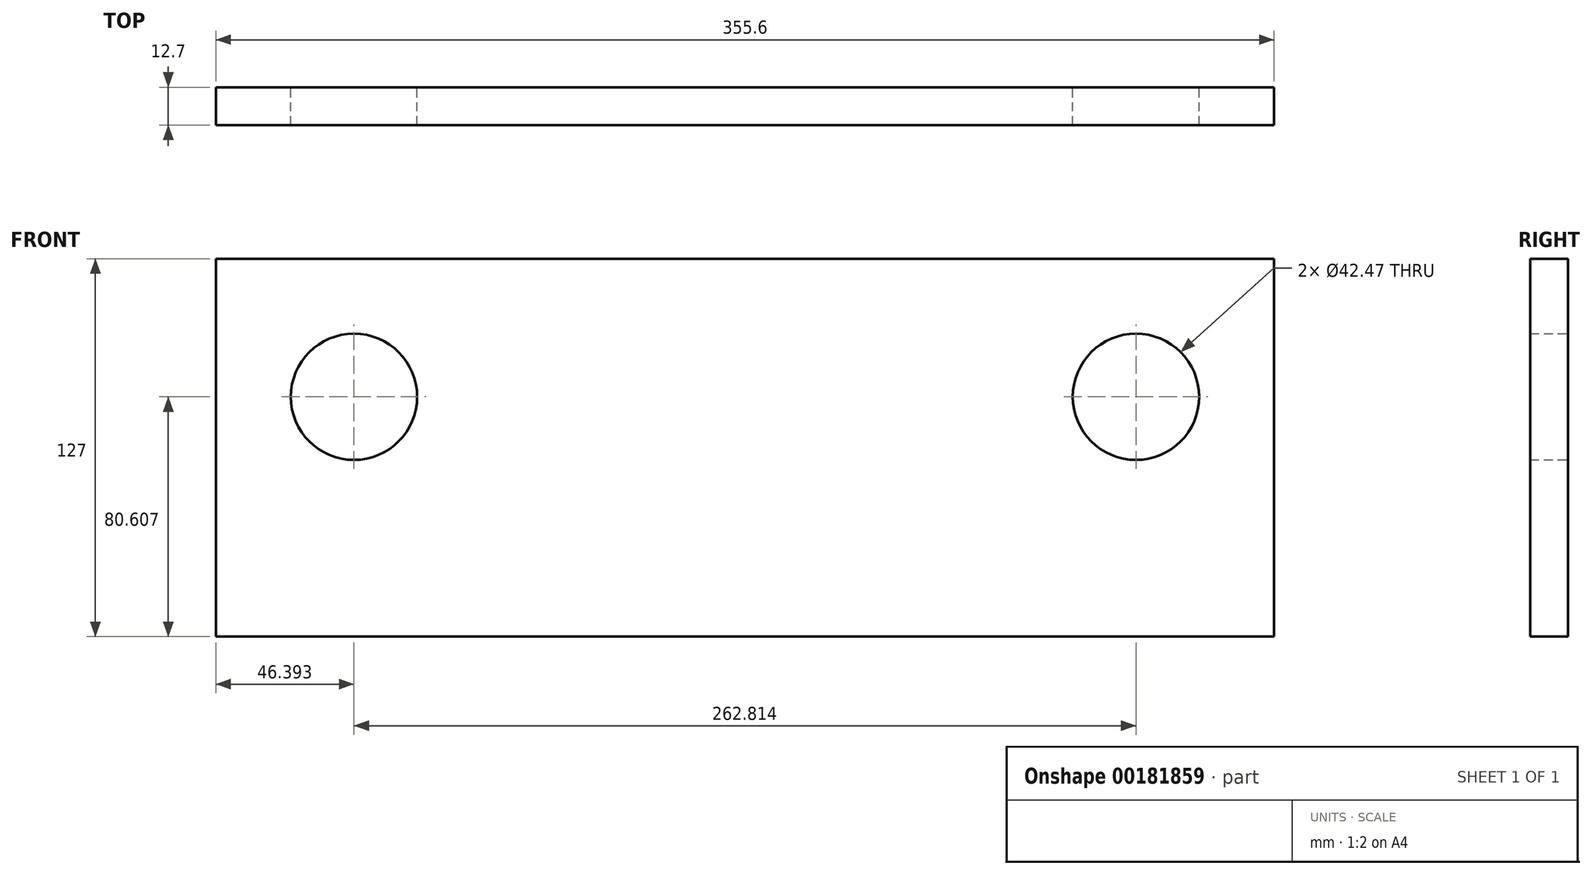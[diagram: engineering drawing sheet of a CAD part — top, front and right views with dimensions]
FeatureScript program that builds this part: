
annotation { "Feature Type Name" : "Feature", "Feature Type Description" : "" }
export const myFeature = defineFeature(function(context is Context, id is Id, definition is map)
    precondition{}
    {
        {
            var Q0;
            Q0=qCreatedBy(makeId("Front.planeOp"),FACE);
            var sketch = newSketch(context, id + "F0", { "sketchPlane" : qUnion([Q0])});
            skLineSegment(sketch, "E0.bottom", {"start": v(177.8, 63.5) * mm, "end": v(-177.8, 63.5) * mm});
            skLineSegment(sketch, "E0.top", {"start": v(177.8, -63.5) * mm, "end": v(-177.8, -63.5) * mm});
            skLineSegment(sketch, "E0.left", {"start": v(177.8, 63.5) * mm, "end": v(177.8, -63.5) * mm});
            skLineSegment(sketch, "E0.right", {"start": v(-177.8, 63.5) * mm, "end": v(-177.8, -63.5) * mm});
            skPoint(sketch, "E0.middle", {"position": v(0, 0) * mm});
            skLineSegment(sketch, "E1.bottom", {"start": v(177.8, 63.5) * mm, "end": v(131.4, 63.5) * mm});
            skLineSegment(sketch, "E1.left", {"start": v(177.8, 63.5) * mm, "end": v(177.8, 17.1) * mm});
            skCircle(sketch, "E2", {"center": v(131.4, 17.1) * mm, "radius": 21.23 * mm});
            skLineSegment(sketch, "E3.bottom", {"start": v(-177.8, 63.5) * mm, "end": v(-131.4, 63.5) * mm});
            skLineSegment(sketch, "E3.left", {"start": v(-177.8, 63.5) * mm, "end": v(-177.8, 17.1) * mm});
            skCircle(sketch, "E4", {"center": v(-131.4, 17.1) * mm, "radius": 21.23 * mm});
            skSolve(sketch);
        }
        {
            var Q0;
            Q0 = qSketchRegion(id + "F0", true);
            extrude(context, id + "F1", {"entities" : qUnion([Q0]), "depth" : 12.7 * mm});
        }
        {
            var Q0;
            Q0 = qSketchRegion(id + "F0", true);
            extrude(context, id + "F2", {"entities" : qUnion([Q0]), "operationType" : NewBodyOperationType.REMOVE, "endBound" : BoundingType.THROUGH_ALL, "oppositeDirection" : true, "depth" : 25.4 * mm});
        }
    });
